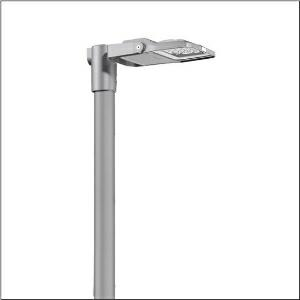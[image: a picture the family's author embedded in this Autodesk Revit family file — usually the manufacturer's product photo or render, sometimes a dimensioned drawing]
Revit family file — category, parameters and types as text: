
# Revit family: floodlight_fl_21_micro___pl61_5xa7761a2c3a_fa04
name_source: partatom
category: Lighting Fixtures
units: mm (PartAtom-declared; Revit-internal decimal feet)

## family parameters
Cut with Voids When Loaded = No
Host = Face
Light Source = No
Part Type = Normal
Room Calculation Point = No
Round Connector Dimension = Use Diameter
Shared = No

## types (1)
- --- (1 x LED, 2910 lm, 23.1 W, 3000K)
    Apparent Load = 23 VA
    CIE Flux Codes = 33 65 98 100 100
    Color Rendering = 70
    Color Temperature = 3000K
    Default Elevation = 1800 mm
    Description = Floodlight FL 21 micro, floodlight, primary light control with lens, of PMMA, primary optical cover: protective disc, of toughened safety glass, transparent, light distribution: PL61, light emission: direct distribution, installation type: surface-mounted, LED, High Power LED, rated luminous flux: 2.910lm, luminous efficacy: 126lm/W, light colour: 730, colour temperature: 3000K, control gear: ECG iQ, control: optimised constant luminous flux control (CLO 2.0), Desk-Remote (wireless, voltage-free reading and setting of iQ features in the workshop via application-optimized NFC function/RFID function), Light-Fading, Smart-Wire, Night-Set, Lumen-Switch, Temp-Guard, Auto-Match, with terminal, 6-pole, mains connection: 220..240V, AC, 50/60Hz, start of lifetime: 23W, end of lifetime: 24W, reduction: 11W, luminaire housing, of diecast aluminium, powder-coated, Siteco® metallic grey (DB 702S), corrosivity category C5 according to DIN EN ISO 12944, mast bracket, of steel, galvanised, powder-coated, Siteco® metallic grey (DB 702S), protection rating (complete): IP66, insulation class (complete): insulation class II (safety insulation), certification: CE, protection symbol: D, impact resistance: IK07, permissible operating ambient temperature: -40..+40°C, permissible operating ambient temperature for outdoor applications: -40..+50°C, standard: DIN EN 12944, packaging unit: 1 piece

Light Distribution: PL61
    Height = 65 mm
    Lamp = 1 x LED
    Lamp Light Flux = 2910 lm
    Lamp Power = 23.1 W
    Lamp count = 1
    Length = 312 mm
    Luminous efficacy = 126 lm/W
    Manufacturer = Siteco
    ModVariant = No
    Model = 5XA7761A2C3A
    Number of Poles = 1
    OnlyDefault = Yes
    Power Factor = 1
    Product Name = Floodlight FL 21 micro | PL61
    Product group = floodlight | pylon top
    ProductGroupID = 6101
    Protection Class = Protection class II
    Protection Degree = IP 66
    RLX_Detail_Level = 1
    RlxData = <blob elided: 101621 chars, md5=e7c8b5fd>
    Socket = socket
    Standby Power = 0 W
    System Light Flux = 2910 lm
    System Power = 23 W
    Type Comments = factory setting: luminous flux: 100 % | dim-lin: 254 | 455 mA
    Type Image = l_1007121.jpg
    URL = http://relux.com
    VarID = @adj_115543
    Voltage = 0 V
    Weight = 0.00 kg
    Width = 230 mm

## geometry (parser evidence)
native form markers: Blend x4, Sweep x12
no freeform markers — native parametric forms only
